# Revit family: Faucet-Lavatory-KOHLER-AVID-97347D_1
name_source: partatom
category: Plumbing Fixtures
revit_build: Autodesk Revit 2017 (Build: 20160225_1515(x64)
units: mm (PartAtom-declared; Revit-internal decimal feet)

## family parameters
Cut with Voids When Loaded = No
Host = Face
OmniClass Number = 23.31.11.00
OmniClass Title = Faucets
Part Type = Normal
Room Calculation Point = No
Round Connector Dimension = Use Diameter
Shared = No

## types (2) — shared parameters
ADA Compliant = No
Assembly Code = D2010
CW Connection = Yes
Cold Water Inlet = Cold Water Inlet
Date Modified = 07/08/2021
Default Elevation = 36"
Faucet Hole Spacing = 0"
Finish = Kohler-Metal-CP-Polished_Chrome
Flow Rate = 2 GPM
HW Connection = Yes
Handle Clearance = 6 1/2"
Height = 9 15/16"
Hot Water Inlet = Hot Water Inlet
Length = 5 7/8"
Manufacturer = KOHLER Co.
Master Format 2014 = 22 41 39
Master Format 2014 Name = Residential Faucets, Supplies, and Trim
Material = Premium Metal Construction
Pressure = 60.00 psi
Product Documentation Link = https://resources.kohler.com
Product Name = AVID
Product Page URL = https://www.kohler.co.uk
Spout Reach = 5 7/8"
URL = https://www.kohler.co.uk
Vent Connection = No
Waste Connection = No
Waste Water Outlet = Waste Water Outlet
WaterSense Certified = No
Width = 2"

## per-type parameters (varying)
| type | Description | Dist1 | Dist2 | Drain Included | Model | Type |
| With Drain, CP-Polished Chrome | Tall single-lever monobloc basin mixer, includes pop-up waste | 7/8" | 2 3/16" | Yes | 97347D-CP | 1 |
| Without Drain, CP-Polished Chrome | Tall single-lever monobloc basin mixer, without waste | 0" | 0" | No | 97347D-ND-CP | 2 |

## geometry (parser evidence)
native form markers: Sweep x3
no freeform markers — native parametric forms only
